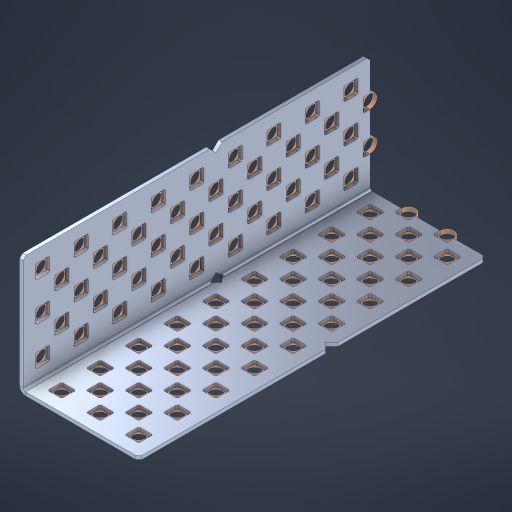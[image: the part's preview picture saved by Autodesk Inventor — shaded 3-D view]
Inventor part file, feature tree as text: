
AUTODESK INVENTOR PART (.ipt)
format: ipt  version: 2023 (Build 270158000, 158)  size: 1,219,072 bytes
history: native  units: in
note: dims shown in document units (in); Inventor stores cm internally (conversion verified against a paired STEP export)
features: other x96, extrude x88, sheet_metal_op x8, sketch x7, pattern_linear x3, mirror x1, chamfer x1
ambient origin geometry x8: Origin, YZ Plane, XZ Plane, XY Plane, X Axis, Y Axis, Z Axis, Center Point
bodies: Solid1 (feature_tree), Body (feature_tree)
feature tree (204):
  sheet_metal_op  "Flanges"
  sheet_metal_op  "Body Pattern"
  pattern_linear  "Center Double"  Spacing1=1.5in  [1 undecoded]
  pattern_linear  "Center Pattern"  Spacing1=0.1875in  [1 undecoded]
  other  "Arc Length"
  pattern_linear  "Notch Pattern"  Spacing1=0.0469in  [1 undecoded]
  other  "Diagonal Plane"
  mirror  "Everything Mirrored"
  chamfer  "End Chamfer"
  sketch  "Sketch1"  dims[d0=1.5in]
  other  "Plate1"
  sketch  "Sketch2"  dims[d1=4.5in]
  other  "Plate2"
  sheet_metal_op  "Bend1"
  sheet_metal_op  "Corner1"
  sketch  "Sketch8"  dims[d2=0.0469in]
  sketch  "Sketch9"  dims[d3=0.0469in]
  other  "Srf91"
  sheet_metal_op  "Body Pattern Sketch"
  other  "Srf92"
  sketch  "Sketch13"  dims[d4=0.0234in]
  sketch  "Sketch15"  dims[d5=0.0938in]
  sketch  "Sketch16"  dims[d6=0.0469in d7=1.5in d8=90.0deg d9=0.0312in d10=0.1875in d11=0.0469in d12=0.0469in d49=0.182in d50=0.02in d52=0.25in d53=0.0469in d54=0.0in d55=0.172in d56=1.0in d57=0.0in d85=0.1473in d86=0.1659in d89=0.0469in d90=0.0in d91=0.04in d92=0.0491in d95=2.5in d96=0.04in d97=0.25in d98=45.0deg d106=0.182in d107=0.02in d110=0.0469in d111=0.0in d112=0.172in d113=0.5in d114=0.0in d117=0.5in d126=0.0491in d127=0.1227in d128=0.08in d129=0.04in d130=2.5in d131=0.25in d132=3.5433in d134=0.5in d135=1.1811in d137=0.5in d140=0.5in d141=1.0in d142=0.3937in d144=0.5in d145=0.071in d146=0.7874in d148=0.5in]
  other  "Srf786"
  other  "Srf856"
  other  "Srf889"
  other  "Srf890"
  other  "Srf891"
  other  "Srf1275"
  other  "Srf1276"
  other  "Srf1278"
  other  "Srf1277"
  other  "Srf1285"
  other  "Srf1286"
  other  "Srf1287"
  other  "Srf1445"
  other  "Srf1446"
  other  "Srf1447"
  other  "Srf1448"
  other  "Srf1449"
  other  "Srf1537"
  other  "Srf1538"
  other  "Srf1539"
  other  "Srf1540"
  other  "Srf1541"
  other  "Srf2009"
  other  "Srf2010"
  other  "Srf2011"
  other  "Srf2012"
  other  "Srf2013"
  other  "Srf2014"
  other  "Srf2015"
  other  "Srf2016"
  other  "Srf2017"
  other  "Srf2043"
  other  "Srf2044"
  other  "Srf2045"
  other  "Srf2046"
  other  "Srf2047"
  other  "Srf2048"
  other  "Srf2049"
  other  "Srf2050"
  other  "Srf2076"
  other  "Srf2077"
  other  "Srf2078"
  other  "Srf2079"
  other  "Srf2080"
  other  "Srf2081"
  other  "Srf2082"
  other  "Srf2083"
  other  "Srf2084"
  other  "Srf2085"
  other  "Srf2086"
  other  "Srf2087"
  other  "Srf2088"
  other  "Srf2089"
  other  "Srf2090"
  other  "Srf2091"
  other  "Srf2092"
  other  "Srf2093"
  other  "Srf2094"
  other  "Srf2095"
  other  "Srf2096"
  other  "Srf2097"
  other  "Srf2098"
  other  "Srf2099"
  other  "Srf2100"
  other  "Srf2179"
  other  "Srf2180"
  other  "Srf2181"
  other  "Srf2182"
  other  "Srf2183"
  other  "Srf2184"
  other  "Srf2185"
  other  "Srf2186"
  other  "Srf2187"
  other  "Srf2188"
  other  "Srf2189"
  other  "Srf2190"
  other  "Srf2191"
  other  "Srf2192"
  other  "Srf2193"
  other  "Srf2194"
  other  "Srf2195"
  other  "Srf2196"
  other  "Srf2197"
  other  "Srf2198"
  other  "Srf2199"
  other  "Srf2200"
  other  "Srf2201"
  other  "Srf2202"
  sheet_metal_op  "Body Stamp"
  sheet_metal_op  "Body Circle"
  other  "Center Stamp"
  other  "Center Circle"
  sheet_metal_op  "Notch"
  extrude  "ExtrusionSrf92"  Depth=0.0469in
  extrude  "ExtrusionSrf856"  Depth=0.182in
  extrude  "ExtrusionSrf889"  Depth=0.02in
  extrude  "ExtrusionSrf890"  Depth=0.25in
  extrude  "ExtrusionSrf891"  Depth=0.0469in
  extrude  "ExtrusionSrf1275"  TaperAngle=0.0deg  [1 undecoded]
  extrude  "ExtrusionSrf1276"  Depth=0.5in
  extrude  "ExtrusionSrf1277"  Depth=0.5in TaperAngle=0.0deg
  extrude  "ExtrusionSrf1345"  Depth=0.5in
  extrude  "ExtrusionSrf1346"  Depth=0.5in
  extrude  "ExtrusionSrf1347"  Depth=0.0469in
  extrude  "ExtrusionSrf1348"  Depth=0.5in TaperAngle=0.0deg
  extrude  "ExtrusionSrf1445"  Depth=0.5in
  extrude  "ExtrusionSrf1446"  Depth=0.25in TaperAngle=45.0deg
  extrude  "ExtrusionSrf1447"  Depth=0.182in
  extrude  "ExtrusionSrf1448"  Depth=0.02in
  extrude  "ExtrusionSrf1449"  Depth=0.0469in
  extrude  "ExtrusionSrf1537"  TaperAngle=0.0deg  [1 undecoded]
  extrude  "ExtrusionSrf1538"  Depth=0.5in
  extrude  "ExtrusionSrf1539"  Depth=0.5in TaperAngle=0.0deg
  extrude  "ExtrusionSrf1540"  Depth=0.5in
  extrude  "ExtrusionSrf1541"  Depth=0.5in
  extrude  "ExtrusionSrf2009"  Depth=0.5in
  extrude  "ExtrusionSrf2010"  Depth=0.5in
  extrude  "ExtrusionSrf2011"  Depth=0.5in
  extrude  "ExtrusionSrf2012"  Depth=0.5in
  extrude  "ExtrusionSrf2013"  Depth=0.25in
  extrude  "ExtrusionSrf2014"  Depth=0.5in
  extrude  "ExtrusionSrf2015"  Depth=0.5in
  extrude  "ExtrusionSrf2016"  Depth=0.5in
  extrude  "ExtrusionSrf2017"  Depth=0.5in
  extrude  "ExtrusionSrf2043"  Depth=0.3937in
  extrude  "ExtrusionSrf2044"  Depth=0.5in
  extrude  "ExtrusionSrf2045"  Depth=0.5in
  extrude  "ExtrusionSrf2046"  [1 undecoded]
  extrude  "ExtrusionSrf2047"  [1 undecoded]
  extrude  "ExtrusionSrf2048"  [1 undecoded]
  extrude  "ExtrusionSrf2049"  [1 undecoded]
  extrude  "ExtrusionSrf2050"  [1 undecoded]
  extrude  "ExtrusionSrf2076"  [1 undecoded]
  extrude  "ExtrusionSrf2077"  [1 undecoded]
  extrude  "ExtrusionSrf2078"  [1 undecoded]
  extrude  "ExtrusionSrf2079"  [1 undecoded]
  extrude  "ExtrusionSrf2080"  [1 undecoded]
  extrude  "ExtrusionSrf2081"  [1 undecoded]
  extrude  "ExtrusionSrf2082"  [1 undecoded]
  extrude  "ExtrusionSrf2083"  [1 undecoded]
  extrude  "ExtrusionSrf2084"  [1 undecoded]
  extrude  "ExtrusionSrf2085"  [1 undecoded]
  extrude  "ExtrusionSrf2086"  [1 undecoded]
  extrude  "ExtrusionSrf2087"  [1 undecoded]
  extrude  "ExtrusionSrf2088"  [1 undecoded]
  extrude  "ExtrusionSrf2089"  [1 undecoded]
  extrude  "ExtrusionSrf2090"  [1 undecoded]
  extrude  "ExtrusionSrf2091"  [1 undecoded]
  extrude  "ExtrusionSrf2092"  [1 undecoded]
  extrude  "ExtrusionSrf2093"  [1 undecoded]
  extrude  "ExtrusionSrf2094"  [1 undecoded]
  extrude  "ExtrusionSrf2095"  [1 undecoded]
  extrude  "ExtrusionSrf2096"  [1 undecoded]
  extrude  "ExtrusionSrf2097"  [1 undecoded]
  extrude  "ExtrusionSrf2098"  [1 undecoded]
  extrude  "ExtrusionSrf2099"  [1 undecoded]
  extrude  "ExtrusionSrf2100"  [1 undecoded]
  extrude  "ExtrusionSrf2179"  [1 undecoded]
  extrude  "ExtrusionSrf2180"  [1 undecoded]
  extrude  "ExtrusionSrf2181"  [1 undecoded]
  extrude  "ExtrusionSrf2182"  [1 undecoded]
  extrude  "ExtrusionSrf2183"  [1 undecoded]
  extrude  "ExtrusionSrf2184"  [1 undecoded]
  extrude  "ExtrusionSrf2185"  [1 undecoded]
  extrude  "ExtrusionSrf2186"  [1 undecoded]
  extrude  "ExtrusionSrf2187"  [1 undecoded]
  extrude  "ExtrusionSrf2188"  [1 undecoded]
  extrude  "ExtrusionSrf2189"  [1 undecoded]
  extrude  "ExtrusionSrf2190"  [1 undecoded]
  extrude  "ExtrusionSrf2191"  [1 undecoded]
  extrude  "ExtrusionSrf2192"  [1 undecoded]
  extrude  "ExtrusionSrf2193"  [1 undecoded]
  extrude  "ExtrusionSrf2194"  [1 undecoded]
  extrude  "ExtrusionSrf2195"  [1 undecoded]
  extrude  "ExtrusionSrf2196"  [1 undecoded]
  extrude  "ExtrusionSrf2197"  [1 undecoded]
  extrude  "ExtrusionSrf2198"  [1 undecoded]
  extrude  "ExtrusionSrf2199"  [1 undecoded]
  extrude  "ExtrusionSrf2200"  [1 undecoded]
  extrude  "ExtrusionSrf2201"  [1 undecoded]
  extrude  "ExtrusionSrf2202"  [1 undecoded]
note: 59 required parameter values undecoded (feature->parameter linkage not recoverable at this tier; creation-order binding heuristic only, values carry confidence <= 0.55)
